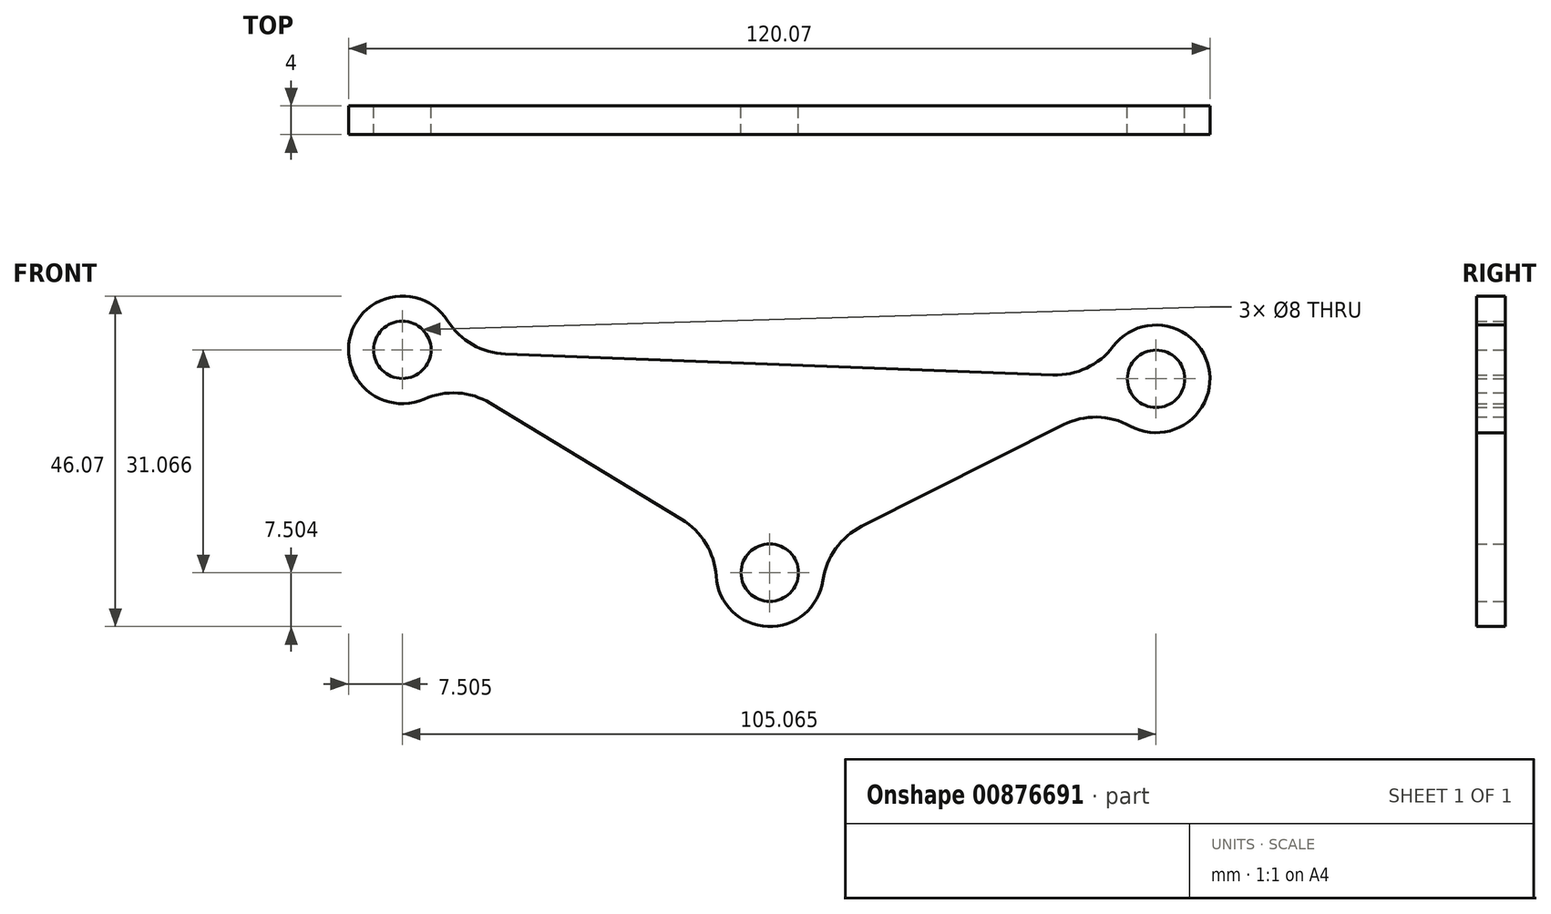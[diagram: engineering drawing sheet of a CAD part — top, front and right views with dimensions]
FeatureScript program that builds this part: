
annotation { "Feature Type Name" : "Feature", "Feature Type Description" : "" }
export const myFeature = defineFeature(function(context is Context, id is Id, definition is map)
    precondition{}
    {
        {
            var Q0;
            Q0=qCreatedBy(makeId("Front.planeOp"),FACE);
            var sketch = newSketch(context, id + "F0", { "sketchPlane" : qUnion([Q0])});
            skCircle(sketch, "E0", {"center": v(-0.58, -31.07) * mm, "radius": 4 * mm});
            skCircle(sketch, "E1", {"center": v(-51.8, 0) * mm, "radius": 4 * mm});
            skCircle(sketch, "E2", {"center": v(53.27, -4.04) * mm, "radius": 4 * mm});
            skArc(sketch, "E3", {"start": v(-44.3, -0.32) * mm, "mid": v(-58.97, 2.17) * mm, "end": v(-45.38, -3.89) * mm});
            skArc(sketch, "E4", {"start": v(-7, -27.18) * mm, "mid": v(-0.88, -38.56) * mm, "end": v(6.11, -27.7) * mm});
            skArc(sketch, "E5", {"start": v(46.53, -7.33) * mm, "mid": v(60.6, -2.5) * mm, "end": v(45.78, -3.76) * mm});
            skLineSegment(sketch, "E6", {"start": v(-45.38, -3.89) * mm, "end": v(-7, -27.18) * mm});
            skLineSegment(sketch, "E7", {"start": v(6.11, -27.7) * mm, "end": v(46.53, -7.33) * mm});
            skLineSegment(sketch, "E8.trimOffspring", {"start": v(45.78, -3.76) * mm, "end": v(-44.3, -0.32) * mm});
            skSolve(sketch);
        }
        {
            var Q0;
            Q0 = qSketchRegion(id + "F0", true);
            extrude(context, id + "F1", {"entities" : qUnion([Q0]), "depth" : 4 * mm, "offsetDistance" : 25 * mm});
        }
        {
            var Q0;
            Q0=makeQuery(id+"F1.opExtrude","SWEPT_EDGE",EDGE,{"disambiguationData":[OSD([sQuery(id+"F0.wireOp",EDGE,"E3"),sQuery(id+"F0.wireOp",EDGE,"E8.trimOffspring")])]});
            var Q1;
            Q1=makeQuery(id+"F1.opExtrude","SWEPT_EDGE",EDGE,{"disambiguationData":[OSD([sQuery(id+"F0.wireOp",EDGE,"E5"),sQuery(id+"F0.wireOp",EDGE,"E8.trimOffspring")])]});
            var Q2;
            Q2=makeQuery(id+"F1.opExtrude","SWEPT_EDGE",EDGE,{"disambiguationData":[OSD([sQuery(id+"F0.wireOp",EDGE,"E5"),sQuery(id+"F0.wireOp",EDGE,"E7")])]});
            var Q3;
            Q3=makeQuery(id+"F1.opExtrude","SWEPT_EDGE",EDGE,{"disambiguationData":[OSD([sQuery(id+"F0.wireOp",EDGE,"E4"),sQuery(id+"F0.wireOp",EDGE,"E7")])]});
            var Q4;
            Q4=makeQuery(id+"F1.opExtrude","SWEPT_EDGE",EDGE,{"disambiguationData":[OSD([sQuery(id+"F0.wireOp",EDGE,"E4"),sQuery(id+"F0.wireOp",EDGE,"E6")])]});
            var Q5;
            Q5=makeQuery(id+"F1.opExtrude","SWEPT_EDGE",EDGE,{"disambiguationData":[OSD([sQuery(id+"F0.wireOp",EDGE,"E3"),sQuery(id+"F0.wireOp",EDGE,"E6")])]});
            fillet(context, id + "F2", {"entities" : qUnion([Q0, Q1, Q2, Q3, Q4, Q5]), "radius" : 10 * mm, "tangentPropagation" : true, "allowEdgeOverflow" : false});
        }
    });
